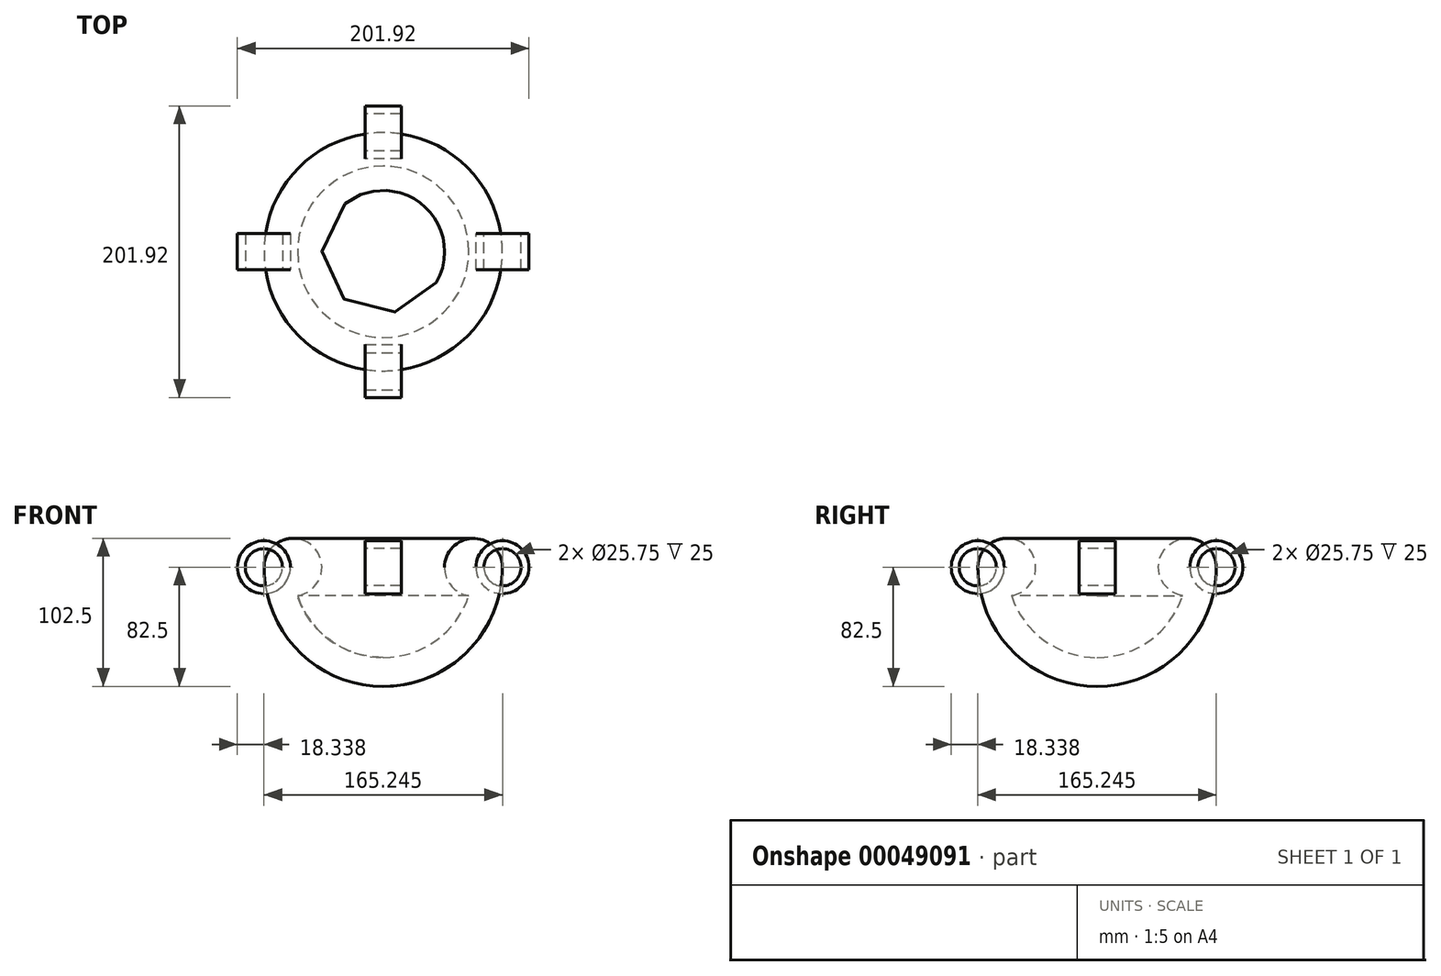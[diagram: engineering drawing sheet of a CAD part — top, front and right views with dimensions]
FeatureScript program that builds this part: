
annotation { "Feature Type Name" : "Feature", "Feature Type Description" : "" }
export const myFeature = defineFeature(function(context is Context, id is Id, definition is map)
    precondition{}
    {
        {
            var Q0;
            Q0=qCreatedBy(makeId("Front.planeOp"),FACE);
            var sketch = newSketch(context, id + "F0", { "sketchPlane" : qUnion([Q0])});
            skArc(sketch, "E0", {"start": v(0, -62.5) * mm, "mid": v(36.55, -50.7) * mm, "end": v(59.3, -19.74) * mm});
            skArc(sketch, "E1", {"start": v(0, -82.5) * mm, "mid": v(58.34, -58.34) * mm, "end": v(82.5, 0) * mm});
            skLineSegment(sketch, "E2", {"start": v(0, 96.88) * mm, "end": v(0, -68.27) * mm, "construction": true});
            skArc(sketch, "E3", {"start": v(82.5, 0) * mm, "mid": v(49.54, 15.23) * mm, "end": v(59.3, -19.74) * mm});
            skLineSegment(sketch, "E4", {"start": v(0, -62.5) * mm, "end": v(0, -82.5) * mm});
            skSolve(sketch);
        }
        {
            var Q0;
            Q0=makeQuery(id+"F0.imprint","IMPRINT",FACE,{"disambiguationData":[TD([[makeQuery(id+"F0.imprint","IMPRINT",EDGE,{"derivedFrom":sQuery(id+"F0.wireOp",EDGE,"E0")}),-1.0]])]});
            var Q1;
            Q1=sQuery(id+"F0.wireOp",EDGE,"E2");
            revolve(context, id + "F1", {"entities" : qUnion([Q0]), "axis" : qUnion([Q1]), "revolveType" : RevolveType.FULL});
        }
        {
            var Q0;
            Q0=qCreatedBy(makeId("Front.planeOp"),FACE);
            var sketch = newSketch(context, id + "F2", { "sketchPlane" : qUnion([Q0])});
            skCircle(sketch, "E5", {"center": v(-82.62, 0) * mm, "radius": 18.34 * mm});
            skCircle(sketch, "E6", {"center": v(-82.62, 0) * mm, "radius": 12.87 * mm});
            skSolve(sketch);
        }
        {
            var Q0;
            Q0=makeQuery(id+"F2.imprint","IMPRINT",FACE,{"disambiguationData":[TD([[makeQuery(id+"F2.imprint","IMPRINT",EDGE,{"derivedFrom":sQuery(id+"F2.wireOp",EDGE,"E5")}),1.0]])]});
            extrude(context, id + "F3", {"entities" : qUnion([Q0]), "endBound" : BoundingType.SYMMETRIC, "oppositeDirection" : true, "depth" : 25 * mm});
        }
        {
            var Q0;
            Q0=makeQuery(id+"F3.opExtrude","SWEPT_BODY",BODY,{"disambiguationData":[OSD([sQuery(id+"F2.wireOp",EDGE,"E5"),sQuery(id+"F2.wireOp",EDGE,"E6")])]});
            var Q1;
            Q1=sQuery(id+"F0.wireOp",EDGE,"E2");
            circularPattern(context, id + "F4", {"entities" : qUnion([Q0]), "axis" : qUnion([Q1]), "angle" : 90 * degree, "instanceCount" : 4});
        }
    });
